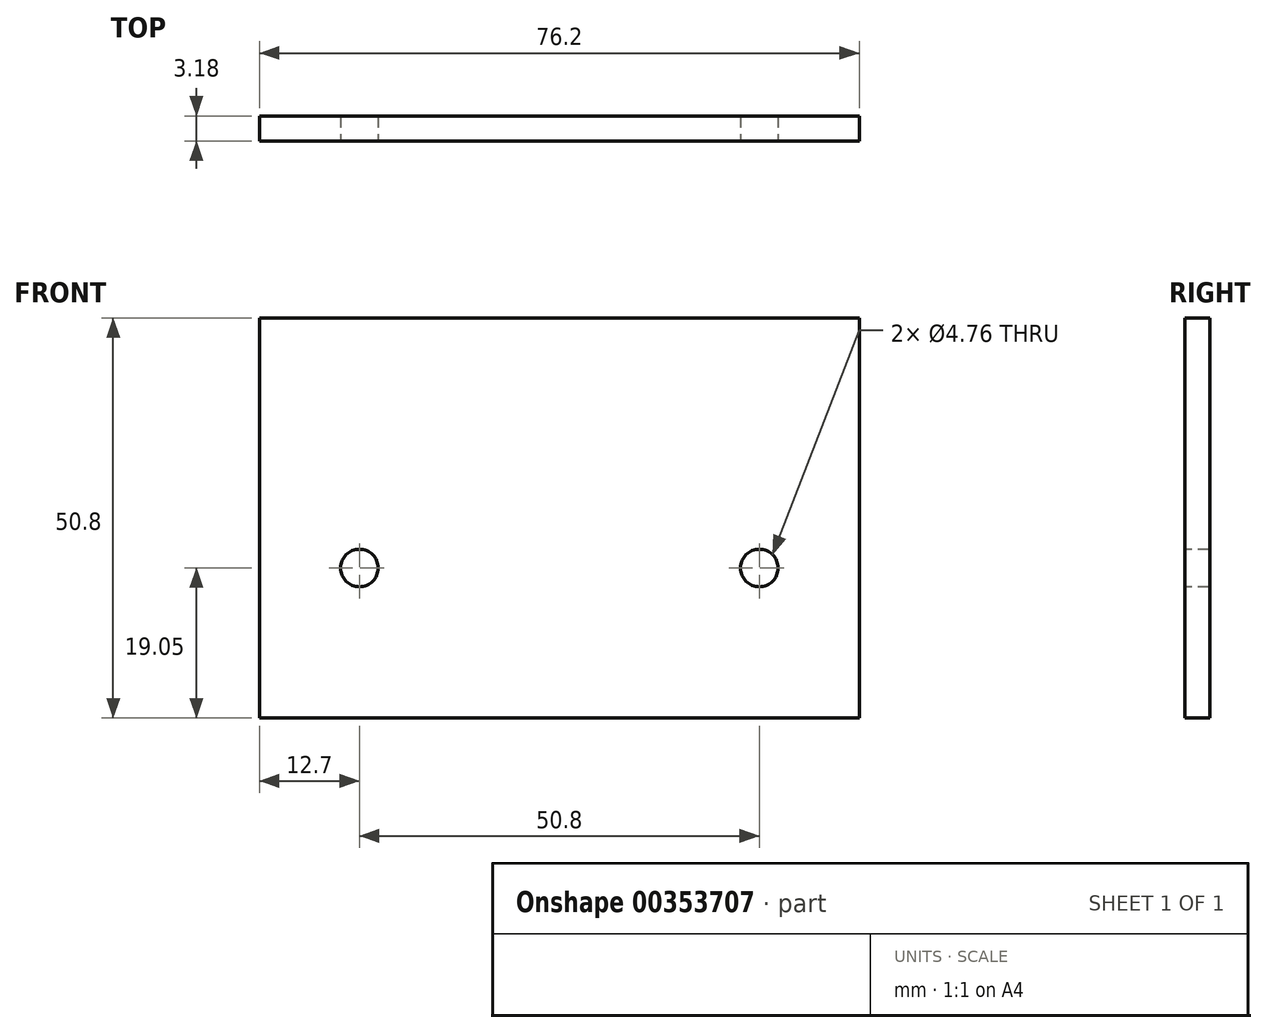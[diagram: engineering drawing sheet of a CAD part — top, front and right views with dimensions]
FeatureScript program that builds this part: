
annotation { "Feature Type Name" : "Feature", "Feature Type Description" : "" }
export const myFeature = defineFeature(function(context is Context, id is Id, definition is map)
    precondition{}
    {
        {
            var Q0;
            Q0=qCreatedBy(makeId("Front.planeOp"),FACE);
            var sketch = newSketch(context, id + "F0", { "sketchPlane" : qUnion([Q0])});
            skLineSegment(sketch, "E0.bottom", {"start": v(38.1, 25.4) * mm, "end": v(-38.1, 25.4) * mm});
            skLineSegment(sketch, "E0.top", {"start": v(38.1, -25.4) * mm, "end": v(-38.1, -25.4) * mm});
            skLineSegment(sketch, "E0.left", {"start": v(38.1, 25.4) * mm, "end": v(38.1, -25.4) * mm});
            skLineSegment(sketch, "E0.right", {"start": v(-38.1, 25.4) * mm, "end": v(-38.1, -25.4) * mm});
            skPoint(sketch, "E0.middle", {"position": v(0, 0) * mm});
            skSolve(sketch);
        }
        {
            var Q0;
            Q0 = qSketchRegion(id + "F0", true);
            extrude(context, id + "F1", {"entities" : qUnion([Q0]), "depth" : 3.17 * mm, "symmetric" : true});
        }
        {
            var Q0;
            Q0=makeQuery(id+"F1.opExtrude","CAP_FACE",FACE,{"disambiguationData":[OSD([sQuery(id+"F0.wireOp",EDGE,"E0.bottom"),sQuery(id+"F0.wireOp",EDGE,"E0.top"),sQuery(id+"F0.wireOp",EDGE,"E0.left"),sQuery(id+"F0.wireOp",EDGE,"E0.right")])],"isStart":false});
            var sketch = newSketch(context, id + "F2", { "sketchPlane" : qUnion([Q0])});
            skLineSegment(sketch, "E1", {"start": v(38.1, -25.4) * mm, "end": v(38.1, -6.35) * mm, "construction": true});
            skLineSegment(sketch, "E2", {"start": v(38.1, -6.35) * mm, "end": v(-38.1, -6.35) * mm, "construction": true});
            skLineSegment(sketch, "E3", {"start": v(-38.1, -25.4) * mm, "end": v(-25.4, -25.4) * mm, "construction": true});
            skLineSegment(sketch, "E4", {"start": v(-25.4, -25.4) * mm, "end": v(-25.4, -6.35) * mm, "construction": true});
            skLineSegment(sketch, "E5", {"start": v(38.1, -25.4) * mm, "end": v(25.4, -25.4) * mm, "construction": true});
            skLineSegment(sketch, "E6", {"start": v(25.4, -25.4) * mm, "end": v(25.4, -6.35) * mm, "construction": true});
            skCircle(sketch, "E7", {"center": v(-25.4, -6.35) * mm, "radius": 2.38 * mm});
            skCircle(sketch, "E8", {"center": v(25.4, -6.35) * mm, "radius": 2.38 * mm});
            skSolve(sketch);
        }
        {
            var Q0;
            Q0 = qSketchRegion(id + "F2", true);
            extrude(context, id + "F3", {"entities" : qUnion([Q0]), "operationType" : NewBodyOperationType.REMOVE, "oppositeDirection" : true, "depth" : 3.17 * mm});
        }
        {
            var Q0;
            Q0 = qSketchRegion(id + "F2", true);
            extrude(context, id + "F4", {"entities" : qUnion([Q0]), "operationType" : NewBodyOperationType.REMOVE, "oppositeDirection" : true, "depth" : 3.17 * mm});
        }
    });
